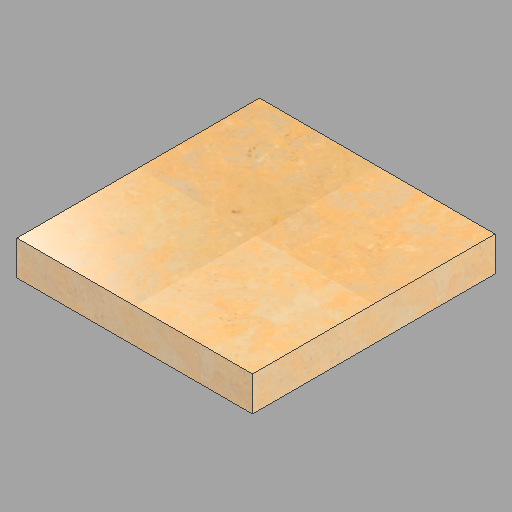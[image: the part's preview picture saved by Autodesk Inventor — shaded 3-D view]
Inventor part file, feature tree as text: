
AUTODESK INVENTOR PART (.ipt)
format: ipt  version: 2022.2 (Build 262287010, 287A)  size: 268,800 bytes
history: native  units: in
note: dims shown in document units (in); Inventor stores cm internally (conversion verified against a paired STEP export)
features: other x1, extrude x1, sketch x1
ambient origin geometry x8: Origin, YZ Plane, XZ Plane, XY Plane, X Axis, Y Axis, Z Axis, Center Point
bodies: Solid1 (feature_tree)
feature tree (3):
  other  "A - Split face veneer - 10"
  extrude  "Extrusion1"  Depth=17.5in
  sketch  "Sketch1"  dims[d0=17.0in d1=17.5in d2=2.5in d3=0.0in]
